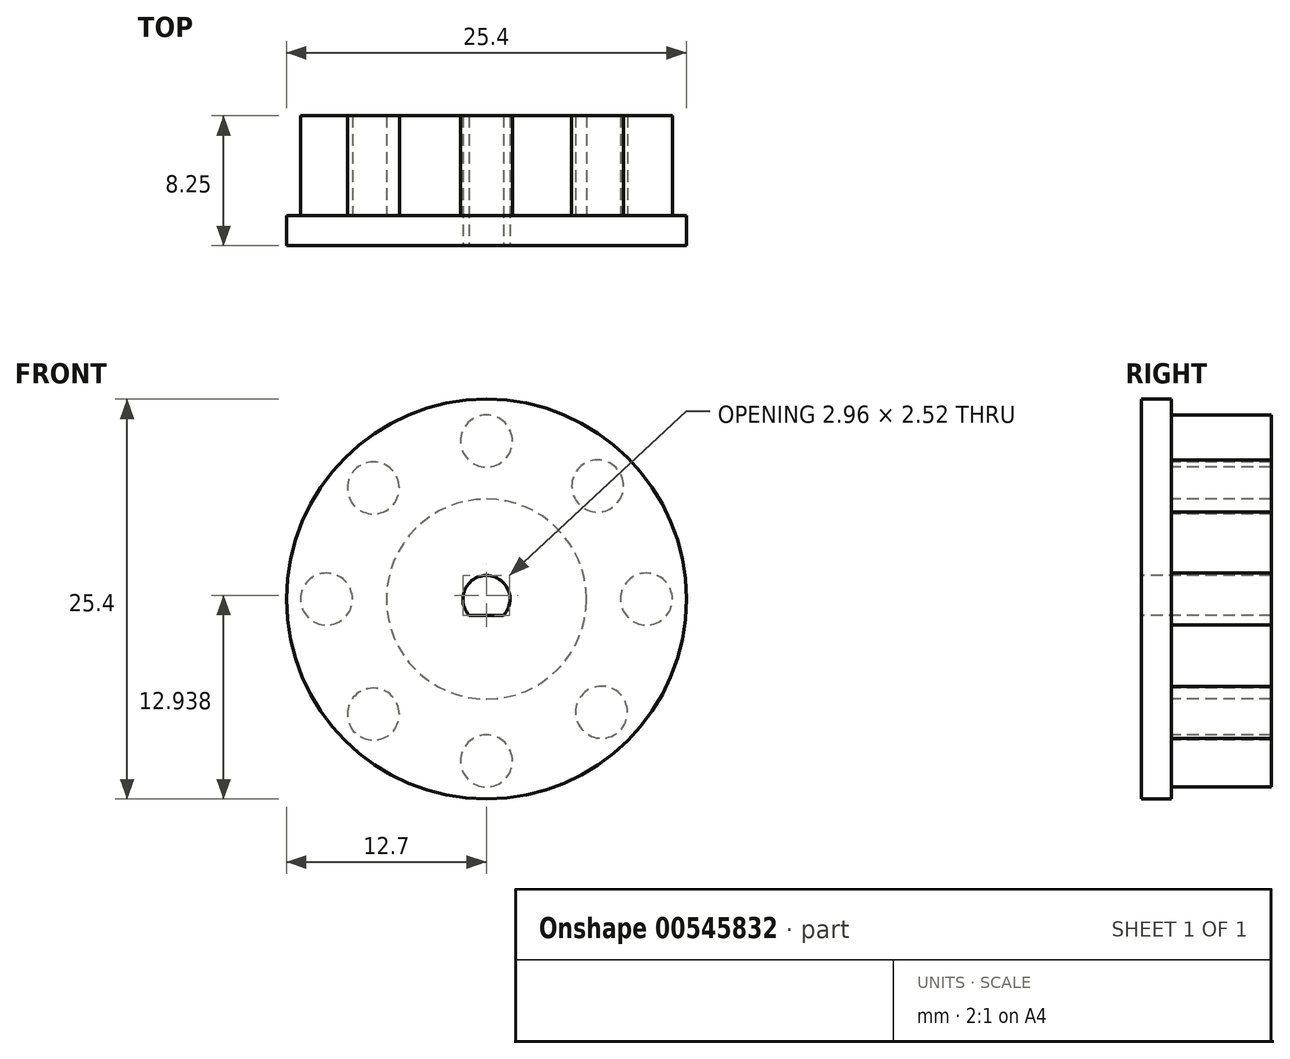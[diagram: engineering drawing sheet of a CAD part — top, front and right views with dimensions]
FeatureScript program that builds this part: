
annotation { "Feature Type Name" : "Feature", "Feature Type Description" : "" }
export const myFeature = defineFeature(function(context is Context, id is Id, definition is map)
    precondition{}
    {
        {
            var Q0;
            Q0=qCreatedBy(makeId("Front.planeOp"),FACE);
            var sketch = newSketch(context, id + "F0", { "sketchPlane" : qUnion([Q0])});
            skCircle(sketch, "E0", {"center": v(0, 0) * mm, "radius": 6.35 * mm});
            skCircle(sketch, "E1", {"center": v(0, 0) * mm, "radius": 12.7 * mm});
            skCircle(sketch, "E2", {"center": v(0, 0) * mm, "radius": 10.16 * mm, "construction": true});
            skArc(sketch, "E3", {"start": v(1.1, -1.02) * mm, "mid": v(0, 1.5) * mm, "end": v(-1.1, -1.02) * mm});
            skLineSegment(sketch, "E4", {"start": v(-1.1, -1.02) * mm, "end": v(1.1, -1.02) * mm});
            skSolve(sketch);
        }
        {
            var Q0;
            Q0=makeQuery(id+"F0.imprint","IMPRINT",FACE,{"disambiguationData":[TD([[makeQuery(id+"F0.imprint","IMPRINT",EDGE,{"derivedFrom":sQuery(id+"F0.wireOp",EDGE,"E0")}),-1.0]])]});
            extrude(context, id + "F1", {"entities" : qUnion([Q0]), "depth" : 1.9 * mm, "offsetDistance" : 25.4 * mm, "symmetric" : true});
        }
        {
            var Q0;
            Q0=makeQuery(id+"F0.imprint","IMPRINT",FACE,{"disambiguationData":[TD([[makeQuery(id+"F0.imprint","IMPRINT",EDGE,{"derivedFrom":sQuery(id+"F0.wireOp",EDGE,"E0")}),1.0]])]});
            extrude(context, id + "F2", {"entities" : qUnion([Q0]), "operationType" : NewBodyOperationType.ADD, "oppositeDirection" : true, "depth" : 7.3 * mm, "offsetDistance" : 25.4 * mm, "hasSecondDirection" : true, "secondDirectionOppositeDirection" : false, "secondDirectionDepth" : 0.95 * mm});
        }
        {
            var Q0;
            {var subQ0=sQuery(id+"F0.wireOp",EDGE,"E0");Q0=makeQuery(id+"F2.boolean.opBoolean","MERGE",FACE,{"derivedFrom":[makeQuery(id+"F1.opExtrude","CAP_FACE",FACE,{"disambiguationData":[OSD([subQ0,sQuery(id+"F0.wireOp",EDGE,"E1")])],"isStart":false}),makeQuery(id+"F2.opExtrude","CAP_FACE",FACE,{"disambiguationData":[OSD([subQ0,sQuery(id+"F0.wireOp",EDGE,"E3"),sQuery(id+"F0.wireOp",EDGE,"E4")])],"isStart":true})]});}
            var sketch = newSketch(context, id + "F3", { "sketchPlane" : qUnion([Q0])});
            skCircle(sketch, "E5", {"center": v(0, -0.12) * mm, "radius": 10.16 * mm, "construction": true});
            skPoint(sketch, "E6", {"position": v(10.16, 0) * mm});
            skPoint(sketch, "E7", {"position": v(-10.16, 0) * mm});
            skPoint(sketch, "E8", {"position": v(0, 10.04) * mm});
            skPoint(sketch, "E8.positionSnap0", {"position": v(0, 1.5) * mm});
            skPoint(sketch, "E9", {"position": v(0, -10.28) * mm});
            skPoint(sketch, "E10", {"position": v(7.06, 7.18) * mm});
            skPoint(sketch, "E11", {"position": v(7.3, -7.18) * mm});
            skPoint(sketch, "E12", {"position": v(-7.18, -7.3) * mm});
            skPoint(sketch, "E13", {"position": v(-7.18, 7.06) * mm});
            skLineSegment(sketch, "E14", {"start": v(0, 0) * mm, "end": v(-7.18, 7.06) * mm, "construction": true});
            skLineSegment(sketch, "E15", {"start": v(0, 0) * mm, "end": v(7.06, 7.18) * mm, "construction": true});
            skLineSegment(sketch, "E16", {"start": v(0, 0) * mm, "end": v(7.3, -7.18) * mm, "construction": true});
            skLineSegment(sketch, "E17", {"start": v(0, 0) * mm, "end": v(-7.18, -7.3) * mm, "construction": true});
            skCircle(sketch, "E18", {"center": v(-10.16, 0) * mm, "radius": 1.65 * mm});
            skCircle(sketch, "E19", {"center": v(-7.18, 7.06) * mm, "radius": 1.65 * mm});
            skCircle(sketch, "E20", {"center": v(0, 10.04) * mm, "radius": 1.65 * mm});
            skCircle(sketch, "E21", {"center": v(7.06, 7.18) * mm, "radius": 1.65 * mm});
            skCircle(sketch, "E22", {"center": v(10.16, 0) * mm, "radius": 1.65 * mm});
            skCircle(sketch, "E23", {"center": v(7.3, -7.18) * mm, "radius": 1.65 * mm});
            skCircle(sketch, "E24", {"center": v(0, -10.28) * mm, "radius": 1.65 * mm});
            skCircle(sketch, "E25", {"center": v(-7.18, -7.3) * mm, "radius": 1.65 * mm});
            skSolve(sketch);
        }
        {
            var Q0;
            Q0=makeQuery(id+"F3.imprint","IMPRINT",FACE,{"disambiguationData":[TD([[makeQuery(id+"F3.imprint","IMPRINT",EDGE,{"derivedFrom":sQuery(id+"F3.wireOp",EDGE,"E20")}),1.0]])]});
            var Q1;
            Q1=makeQuery(id+"F3.imprint","IMPRINT",FACE,{"disambiguationData":[TD([[makeQuery(id+"F3.imprint","IMPRINT",EDGE,{"derivedFrom":sQuery(id+"F3.wireOp",EDGE,"E21")}),1.0]])]});
            var Q2;
            Q2=makeQuery(id+"F3.imprint","IMPRINT",FACE,{"disambiguationData":[TD([[makeQuery(id+"F3.imprint","IMPRINT",EDGE,{"derivedFrom":sQuery(id+"F3.wireOp",EDGE,"E23")}),1.0]])]});
            var Q3;
            Q3=makeQuery(id+"F3.imprint","IMPRINT",FACE,{"disambiguationData":[TD([[makeQuery(id+"F3.imprint","IMPRINT",EDGE,{"derivedFrom":sQuery(id+"F3.wireOp",EDGE,"E24")}),1.0]])]});
            var Q4;
            Q4=makeQuery(id+"F3.imprint","IMPRINT",FACE,{"disambiguationData":[TD([[makeQuery(id+"F3.imprint","IMPRINT",EDGE,{"derivedFrom":sQuery(id+"F3.wireOp",EDGE,"E22")}),1.0]])]});
            var Q5;
            Q5=makeQuery(id+"F3.imprint","IMPRINT",FACE,{"disambiguationData":[TD([[makeQuery(id+"F3.imprint","IMPRINT",EDGE,{"derivedFrom":sQuery(id+"F3.wireOp",EDGE,"E19")}),1.0]])]});
            var Q6;
            Q6=makeQuery(id+"F3.imprint","IMPRINT",FACE,{"disambiguationData":[TD([[makeQuery(id+"F3.imprint","IMPRINT",EDGE,{"derivedFrom":sQuery(id+"F3.wireOp",EDGE,"E18")}),1.0]])]});
            var Q7;
            Q7=makeQuery(id+"F3.imprint","IMPRINT",FACE,{"disambiguationData":[TD([[makeQuery(id+"F3.imprint","IMPRINT",EDGE,{"derivedFrom":sQuery(id+"F3.wireOp",EDGE,"E25")}),1.0]])]});
            extrude(context, id + "F4", {"entities" : qUnion([Q0, Q1, Q2, Q3, Q4, Q5, Q6, Q7]), "operationType" : NewBodyOperationType.ADD, "oppositeDirection" : true, "depth" : 8.25 * mm, "offsetDistance" : 25.4 * mm});
        }
    });
